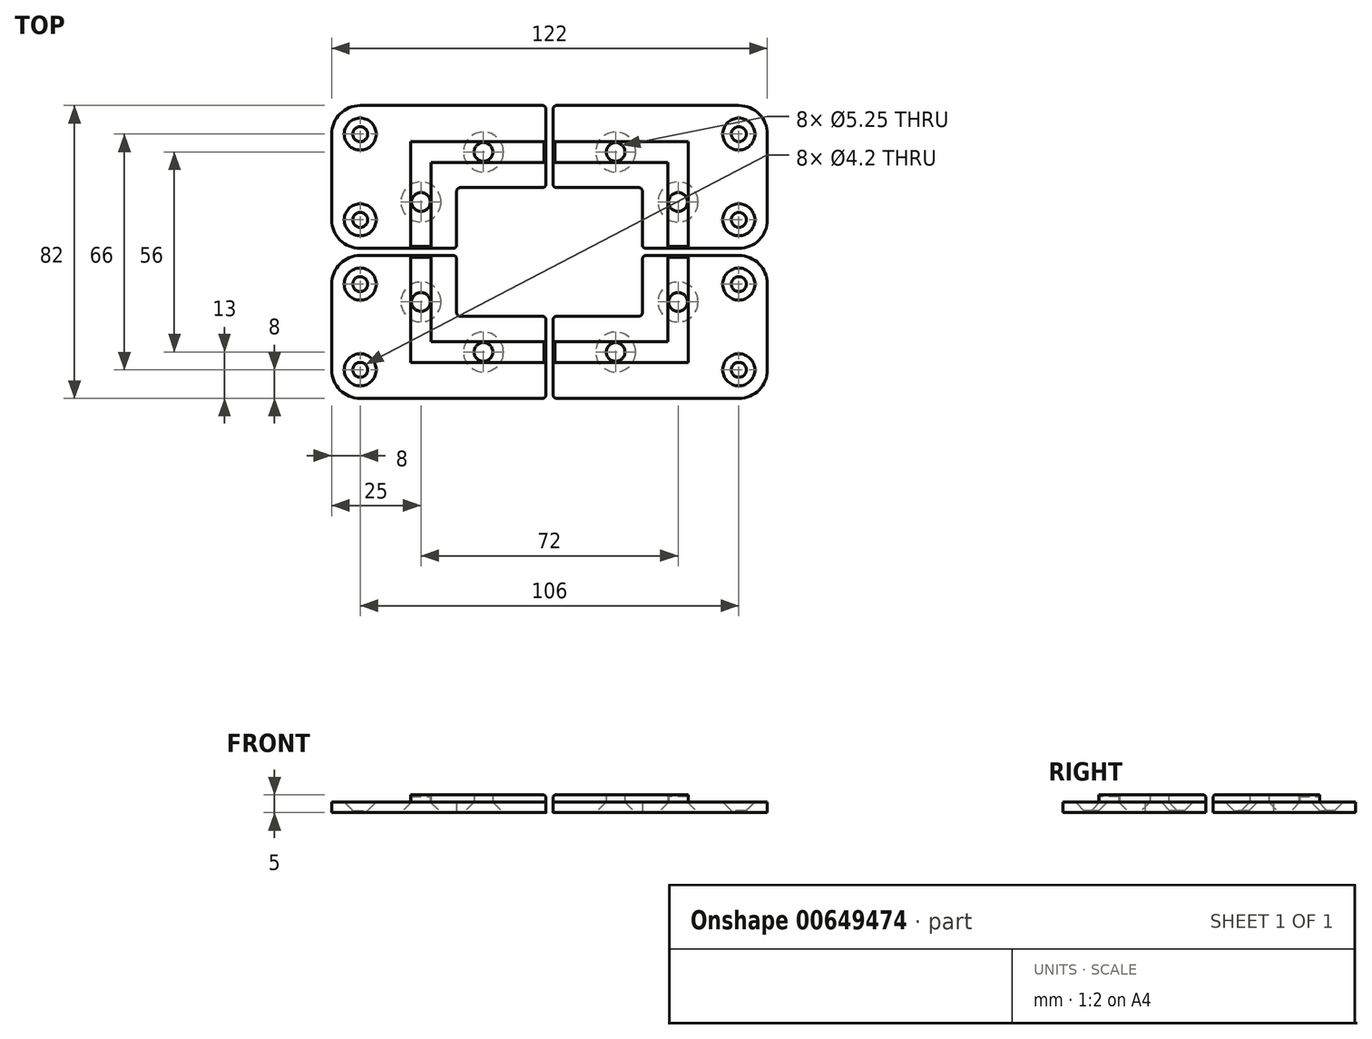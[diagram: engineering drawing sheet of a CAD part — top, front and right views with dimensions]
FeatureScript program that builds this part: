
annotation { "Feature Type Name" : "Feature", "Feature Type Description" : "" }
export const myFeature = defineFeature(function(context is Context, id is Id, definition is map)
    precondition{}
    {
        {
            var Q0;
            Q0=qCreatedBy(makeId("Top.planeOp"),FACE);
            var sketch = newSketch(context, id + "F0", { "sketchPlane" : qUnion([Q0])});
            skLineSegment(sketch, "E0.bottom", {"start": v(1, 1) * mm, "end": v(61, 1) * mm});
            skLineSegment(sketch, "E0.top", {"start": v(1, 41) * mm, "end": v(61, 41) * mm});
            skLineSegment(sketch, "E0.left", {"start": v(1, 1) * mm, "end": v(1, 41) * mm});
            skLineSegment(sketch, "E0.right", {"start": v(61, 1) * mm, "end": v(61, 41) * mm});
            skLineSegment(sketch, "E1", {"start": v(1, 38) * mm, "end": v(46, 38) * mm, "construction": true});
            skLineSegment(sketch, "E2", {"start": v(46, 38) * mm, "end": v(46, 1) * mm, "construction": true});
            skLineSegment(sketch, "E3.0", {"start": v(26, 18) * mm, "end": v(26, -13.7) * mm});
            skLineSegment(sketch, "E3.1", {"start": v(0, 18) * mm, "end": v(26, 18) * mm});
            skLineSegment(sketch, "E4", {"start": v(1, 28) * mm, "end": v(36, 28) * mm, "construction": true});
            skLineSegment(sketch, "E5", {"start": v(36, 28) * mm, "end": v(36, 0) * mm, "construction": true});
            skLineSegment(sketch, "E6.0", {"start": v(33.1, 25.1) * mm, "end": v(33.1, 0) * mm});
            skLineSegment(sketch, "E6.1", {"start": v(0, 25.1) * mm, "end": v(33.1, 25.1) * mm});
            skLineSegment(sketch, "E7.0", {"start": v(38.9, 30.9) * mm, "end": v(38.9, 0) * mm});
            skLineSegment(sketch, "E7.1", {"start": v(0, 30.9) * mm, "end": v(38.9, 30.9) * mm});
            skPoint(sketch, "E8", {"position": v(36, 14) * mm});
            skPoint(sketch, "E9", {"position": v(18.5, 28) * mm});
            skPoint(sketch, "E10", {"position": v(53, 9) * mm});
            skPoint(sketch, "E11", {"position": v(53, 33) * mm});
            skLineSegment(sketch, "E12", {"start": v(53, 9) * mm, "end": v(53, 33) * mm, "construction": true});
            skSolve(sketch);
        }
        {
            var Q0;
            {var subQ1=sQuery(id+"F0.wireOp",EDGE,"E0.top");Q0=makeQuery(id+"F0.imprint","IMPRINT",FACE,{"disambiguationData":[TD([[makeQuery(id+"F0.imprint","IMPRINT",EDGE,{"derivedFrom":subQ1}),-1.0]])]});}
            var Q1;
            {var subQ0=sQuery(id+"F0.wireOp",EDGE,"E3.1");Q1=makeQuery(id+"F0.imprint","IMPRINT",FACE,{"disambiguationData":[TD([[makeQuery(id+"F0.imprint","IMPRINT",EDGE,{"derivedFrom":subQ0}),1.0]])]});}
            var Q2;
            {var subQ1=sQuery(id+"F0.wireOp",EDGE,"E6.0");Q2=makeQuery(id+"F0.imprint","IMPRINT",FACE,{"disambiguationData":[TD([[makeQuery(id+"F0.imprint","IMPRINT",EDGE,{"derivedFrom":subQ1}),1.0]])]});}
            extrude(context, id + "F1", {"entities" : qUnion([Q0, Q1, Q2]), "depth" : 3 * mm, "offsetDistance" : 25 * mm});
        }
        {
            var Q0;
            {var subQ1=sQuery(id+"F0.wireOp",EDGE,"E6.0");Q0=makeQuery(id+"F0.imprint","IMPRINT",FACE,{"disambiguationData":[TD([[makeQuery(id+"F0.imprint","IMPRINT",EDGE,{"derivedFrom":subQ1}),1.0]])]});}
            extrude(context, id + "F2", {"entities" : qUnion([Q0]), "operationType" : NewBodyOperationType.ADD, "depth" : 5 * mm, "offsetDistance" : 25 * mm});
        }
        {
            var Q0;
            Q0=sQuery(id+"F0.wireOp",VERTEX,"E8");
            var Q1;
            Q1=sQuery(id+"F0.wireOp",VERTEX,"E9");
            var Q2;
            Q2=makeQuery(id+"F1.opExtrude","SWEPT_BODY",BODY,{"disambiguationData":[OSD([sQuery(id+"F0.wireOp",EDGE,"E0.bottom"),sQuery(id+"F0.wireOp",EDGE,"E0.top"),sQuery(id+"F0.wireOp",EDGE,"E0.left"),sQuery(id+"F0.wireOp",EDGE,"E0.right"),sQuery(id+"F0.wireOp",EDGE,"E3.0"),sQuery(id+"F0.wireOp",EDGE,"E3.1")])]});
            hole(context, id + "F3", {"style" : HoleStyle.C_SINK, "endStyle" : HoleEndStyle.THROUGH, "oppositeDirection" : true, "standardTappedOrClearance" : lookupTablePath({ "standard" : "ISO", "fit" : "Close", "size" : "M5", "type" : "Clearance" }), "standardBlindInLast" : lookupTablePath({ "fit" : "Close", "standard" : "ISO", "size" : "M5", "type" : "Clearance" }), "holeDiameter" : 5.25 * mm, "cSinkDiameter" : 11.2 * mm, "cSinkAngle" : 90 * degree, "majorDiameter" : 5 * mm, "isTappedThrough" : true, "tappedDepth" : 12 * mm, "tapClearance" : 3, "startFromSketch" : true, "locations" : qUnion([Q0, Q1]), "scope" : qUnion([Q2])});
        }
        {
            var Q0;
            {var subQ0=sQuery(id+"F0.wireOp",EDGE,"E0.left");var subQ1=sQuery(id+"F0.wireOp",EDGE,"E0.bottom");var subQ2=sQuery(id+"F0.wireOp",EDGE,"E0.top");var subQ3=sQuery(id+"F0.wireOp",EDGE,"E0.right");Q0=makeQuery(id+"F2.boolean.opBoolean","SPLIT",FACE,{"disambiguationData":[TD([makeQuery(id+"F1.opExtrude","SWEPT_FACE",FACE,{"disambiguationData":[OSD([subQ2])]})])],"derivedFrom":makeQuery(id+"F1.opExtrude","CAP_FACE",FACE,{"disambiguationData":[OSD([subQ1,subQ2,subQ0,subQ3,sQuery(id+"F0.wireOp",EDGE,"E3.0"),sQuery(id+"F0.wireOp",EDGE,"E3.1")])],"isStart":false})});}
            var sketch = newSketch(context, id + "F4", { "sketchPlane" : qUnion([Q0])});
            skPoint(sketch, "E13.0", {"position": v(53, 9) * mm});
            skPoint(sketch, "E13.1", {"position": v(53, 33) * mm});
            skSolve(sketch);
        }
        {
            var Q0;
            Q0=sQuery(id+"F4.wireOp",VERTEX,"E13.0");
            var Q1;
            Q1=sQuery(id+"F4.wireOp",VERTEX,"E13.1");
            var Q2;
            Q2=makeQuery(id+"F1.opExtrude","SWEPT_BODY",BODY,{"disambiguationData":[OSD([sQuery(id+"F0.wireOp",EDGE,"E0.bottom"),sQuery(id+"F0.wireOp",EDGE,"E0.top"),sQuery(id+"F0.wireOp",EDGE,"E0.left"),sQuery(id+"F0.wireOp",EDGE,"E0.right"),sQuery(id+"F0.wireOp",EDGE,"E3.0"),sQuery(id+"F0.wireOp",EDGE,"E3.1")])]});
            hole(context, id + "F5", {"style" : HoleStyle.C_SINK, "endStyle" : HoleEndStyle.THROUGH, "standardTappedOrClearance" : lookupTablePath({ "standard" : "ISO", "fit" : "Close", "size" : "M4", "type" : "Clearance" }), "standardBlindInLast" : lookupTablePath({ "fit" : "Close", "standard" : "ISO", "size" : "M4", "type" : "Clearance" }), "holeDiameter" : 4.2 * mm, "cSinkDiameter" : 8.96 * mm, "cSinkAngle" : 90 * degree, "majorDiameter" : 5 * mm, "isTappedThrough" : true, "tappedDepth" : 12 * mm, "tapClearance" : 3, "startFromSketch" : true, "locations" : qUnion([Q0, Q1]), "scope" : qUnion([Q2])});
        }
        {
            var Q0;
            Q0=makeQuery(id+"F1.opExtrude","SWEPT_EDGE",EDGE,{"disambiguationData":[OSD([sQuery(id+"F0.wireOp",EDGE,"E0.top"),sQuery(id+"F0.wireOp",EDGE,"E0.right")])]});
            var Q1;
            Q1=makeQuery(id+"F1.opExtrude","SWEPT_EDGE",EDGE,{"disambiguationData":[OSD([sQuery(id+"F0.wireOp",EDGE,"E0.bottom"),sQuery(id+"F0.wireOp",EDGE,"E0.right")])]});
            fillet(context, id + "F6", {"entities" : qUnion([Q0, Q1]), "radius" : 8 * mm, "tangentPropagation" : true, "allowEdgeOverflow" : false});
        }
        {
            var Q0;
            Q0=makeQuery(id+"F1.opExtrude","SWEPT_EDGE",EDGE,{"disambiguationData":[OSD([sQuery(id+"F0.wireOp",EDGE,"E0.bottom"),sQuery(id+"F0.wireOp",EDGE,"E3.0")])]});
            var Q1;
            Q1=makeQuery(id+"F1.opExtrude","SWEPT_EDGE",EDGE,{"disambiguationData":[OSD([sQuery(id+"F0.wireOp",EDGE,"E3.0"),sQuery(id+"F0.wireOp",EDGE,"E3.1")])]});
            var Q2;
            Q2=makeQuery(id+"F1.opExtrude","SWEPT_EDGE",EDGE,{"disambiguationData":[OSD([sQuery(id+"F0.wireOp",EDGE,"E0.left"),sQuery(id+"F0.wireOp",EDGE,"E3.1")])]});
            var Q3;
            Q3=makeQuery(id+"F1.opExtrude","SWEPT_EDGE",EDGE,{"disambiguationData":[OSD([sQuery(id+"F0.wireOp",EDGE,"E0.top"),sQuery(id+"F0.wireOp",EDGE,"E0.left")])]});
            fillet(context, id + "F7", {"entities" : qUnion([Q0, Q1, Q2, Q3]), "radius" : 1 * mm, "tangentPropagation" : true, "allowEdgeOverflow" : false});
        }
        {
            var Q0;
            Q0=makeQuery(id+"F2.opExtrude","CAP_EDGE",EDGE,{"disambiguationData":[OSD([sQuery(id+"F0.wireOp",EDGE,"E0.bottom")])],"isStart":false});
            var Q1;
            Q1=makeQuery(id+"F2.opExtrude","CAP_EDGE",EDGE,{"disambiguationData":[OSD([sQuery(id+"F0.wireOp",EDGE,"E0.left")])],"isStart":false});
            chamfer(context, id + "F8", {"entities" : qUnion([Q0, Q1]), "width" : 0.5 * mm, "tangentPropagation" : true});
        }
        {
            var Q0;
            Q0=makeQuery(id+"F1.opExtrude","SWEPT_BODY",BODY,{"disambiguationData":[OSD([sQuery(id+"F0.wireOp",EDGE,"E0.bottom"),sQuery(id+"F0.wireOp",EDGE,"E0.top"),sQuery(id+"F0.wireOp",EDGE,"E0.left"),sQuery(id+"F0.wireOp",EDGE,"E0.right"),sQuery(id+"F0.wireOp",EDGE,"E3.0"),sQuery(id+"F0.wireOp",EDGE,"E3.1")])]});
            var Q1;
            Q1=qCreatedBy(makeId("Right.planeOp"),FACE);
            mirror(context, id + "F9", {"entities" : qUnion([Q0]), "mirrorPlane" : qUnion([Q1])});
        }
        {
            var Q0;
            Q0=makeQuery(id+"F9.opPattern","COPY",BODY,{"derivedFrom":makeQuery(id+"F1.opExtrude","SWEPT_BODY",BODY,{"disambiguationData":[OSD([sQuery(id+"F0.wireOp",EDGE,"E0.bottom"),sQuery(id+"F0.wireOp",EDGE,"E0.top"),sQuery(id+"F0.wireOp",EDGE,"E0.left"),sQuery(id+"F0.wireOp",EDGE,"E0.right"),sQuery(id+"F0.wireOp",EDGE,"E3.0"),sQuery(id+"F0.wireOp",EDGE,"E3.1")])]}),"instanceName":"1"});
            var Q1;
            Q1=makeQuery(id+"F1.opExtrude","SWEPT_BODY",BODY,{"disambiguationData":[OSD([sQuery(id+"F0.wireOp",EDGE,"E0.bottom"),sQuery(id+"F0.wireOp",EDGE,"E0.top"),sQuery(id+"F0.wireOp",EDGE,"E0.left"),sQuery(id+"F0.wireOp",EDGE,"E0.right"),sQuery(id+"F0.wireOp",EDGE,"E3.0"),sQuery(id+"F0.wireOp",EDGE,"E3.1")])]});
            var Q2;
            Q2=qCreatedBy(makeId("Front.planeOp"),FACE);
            mirror(context, id + "F10", {"entities" : qUnion([Q0, Q1]), "mirrorPlane" : qUnion([Q2])});
        }
    });
